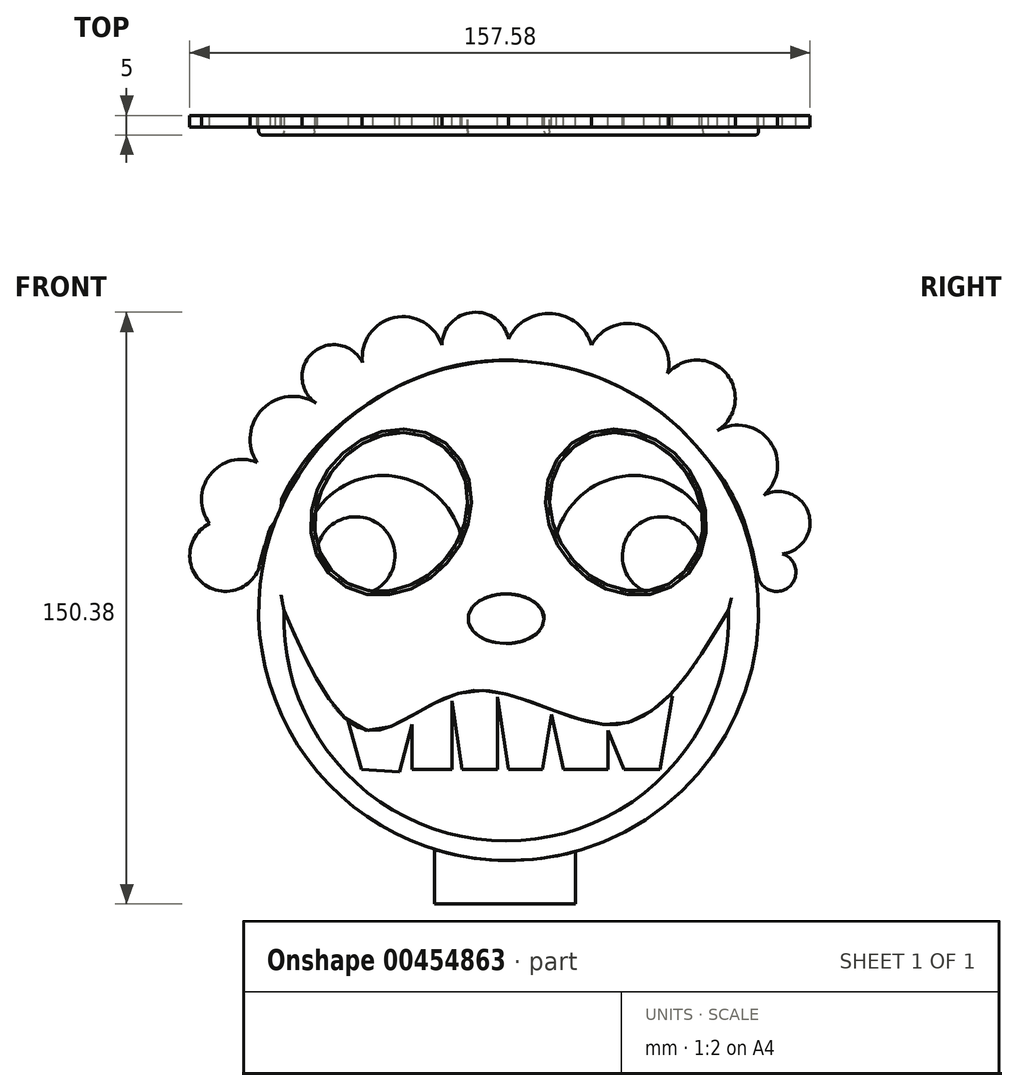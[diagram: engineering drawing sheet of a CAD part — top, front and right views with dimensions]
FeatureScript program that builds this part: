
annotation { "Feature Type Name" : "Feature", "Feature Type Description" : "" }
export const myFeature = defineFeature(function(context is Context, id is Id, definition is map)
    precondition{}
    {
        {
            var Q0;
            Q0=qCreatedBy(makeId("Front.planeOp"),FACE);
            var sketch = newSketch(context, id + "F0", { "sketchPlane" : qUnion([Q0])});
            skCircle(sketch, "E0", {"center": v(0, 0) * mm, "radius": 63.5 * mm});
            skEllipse(sketch, "E1", {"center": v(29.86, 25.05) * mm, "majorRadius": 21.26 * mm, "minorRadius": 18.23 * mm, "majorAxis": v(-0.62, 0.79)});
            skEllipse(sketch, "E2.MirrorC", {"center": v(-29.86, 25.05) * mm, "majorRadius": 21.26 * mm, "minorRadius": 18.23 * mm, "majorAxis": v(0.62, 0.79)});
            skArc(sketch, "E3", {"start": v(-58.71, 0) * mm, "mid": v(0, -58.71) * mm, "end": v(58.71, 0) * mm});
            skSolve(sketch);
        }
        {
            var Q0;
            Q0=makeQuery(id+"F0.imprint","IMPRINT",FACE,{"disambiguationData":[TD([[makeQuery(id+"F0.imprint","IMPRINT",EDGE,{"derivedFrom":sQuery(id+"F0.wireOp",EDGE,"E0")}),1.0]])]});
            extrude(context, id + "F1", {"entities" : qUnion([Q0]), "depth" : 5 * mm});
        }
        {
            var Q0;
            Q0=makeQuery(id+"F1.opExtrude","CAP_FACE",FACE,{"disambiguationData":[OSD([sQuery(id+"F0.wireOp",EDGE,"E0"),sQuery(id+"F0.wireOp",EDGE,"E1"),sQuery(id+"F0.wireOp",EDGE,"E2.MirrorC")])],"isStart":false});
            var sketch = newSketch(context, id + "F2", { "sketchPlane" : qUnion([Q0])});
            skArc(sketch, "E4", {"start": v(-57.08, 0) * mm, "mid": v(-0.64, -58.53) * mm, "end": v(55.8, 0) * mm});
            skEllipse(sketch, "E5", {"center": v(-0.64, -2.06) * mm, "majorRadius": 9.67 * mm, "minorRadius": 6.3 * mm, "majorAxis": v(1, 0)});
            skFitSpline(sketch, "E6", {"points": [v(-57.08, 0) * mm, v(-35.37, -30.5) * mm, v(-9.37, -20.35) * mm, v(27.73, -28.9) * mm, v(55.8, 0) * mm], "startDerivative": vector(78.01, -174.23) * mm, "endDerivative": vector(93.96, 156.78) * mm});
            skCircle(sketch, "E7", {"center": v(0, 59.87) * mm, "radius": 3.39 * mm});
            skSolve(sketch);
        }
        {
            var Q0;
            Q0=makeQuery(id+"F2.imprint","IMPRINT",FACE,{"disambiguationData":[TD([[makeQuery(id+"F2.imprint","IMPRINT",EDGE,{"derivedFrom":sQuery(id+"F2.wireOp",EDGE,"E5")}),1.0]])]});
            var Q1;
            Q1=makeQuery(id+"F2.imprint","IMPRINT",FACE,{"disambiguationData":[TD([[makeQuery(id+"F2.imprint","IMPRINT",EDGE,{"derivedFrom":sQuery(id+"F2.wireOp",EDGE,"E4")}),1.0]])]});
            extrude(context, id + "F3", {"entities" : qUnion([Q0, Q1]), "operationType" : NewBodyOperationType.REMOVE, "oppositeDirection" : true, "depth" : 5 * mm});
        }
        {
            var Q0;
            Q0=qCreatedBy(makeId("Front.planeOp"),FACE);
            var sketch = newSketch(context, id + "F4", { "sketchPlane" : qUnion([Q0])});
            skArc(sketch, "E8", {"start": v(-75.95, 22.14) * mm, "mid": v(-78.18, 7.4) * mm, "end": v(-63.59, 10.4) * mm});
            skArc(sketch, "E9", {"start": v(-63.27, 37.36) * mm, "mid": v(-74.74, 20.8) * mm, "end": v(-59.15, 33.56) * mm});
            skArc(sketch, "E10", {"start": v(-48.68, 52.58) * mm, "mid": v(-64.32, 48.79) * mm, "end": v(-59.15, 33.56) * mm});
            skArc(sketch, "E11", {"start": v(-36.32, 60.19) * mm, "mid": v(-48.64, 66.35) * mm, "end": v(-48.68, 52.58) * mm});
            skArc(sketch, "E12", {"start": v(-16.98, 67.48) * mm, "mid": v(-30.5, 74.02) * mm, "end": v(-36.32, 60.19) * mm});
            skArc(sketch, "E13", {"start": v(0, 69.07) * mm, "mid": v(-9.2, 75.78) * mm, "end": v(-16.98, 67.48) * mm});
            skArc(sketch, "E14", {"start": v(21.07, 67.48) * mm, "mid": v(11.08, 75.49) * mm, "end": v(0, 69.07) * mm});
            skArc(sketch, "E15", {"start": v(40.4, 60.19) * mm, "mid": v(33.94, 72.32) * mm, "end": v(21.07, 67.48) * mm});
            skArc(sketch, "E16", {"start": v(52.78, 45.6) * mm, "mid": v(55.26, 60.25) * mm, "end": v(40.4, 60.19) * mm});
            skArc(sketch, "E17", {"start": v(63.24, 28.17) * mm, "mid": v(66.89, 42.21) * mm, "end": v(52.78, 45.6) * mm});
            skArc(sketch, "E18", {"start": v(67.04, 14.53) * mm, "mid": v(76.28, 24.46) * mm, "end": v(63.24, 28.17) * mm});
            skArc(sketch, "E19", {"start": v(63.24, 9.14) * mm, "mid": v(72.07, 6.94) * mm, "end": v(67.04, 14.53) * mm});
            skFitSpline(sketch, "E20", {"points": [v(-63.59, 10.4) * mm, v(-50.59, 39.58) * mm, v(0, 63.68) * mm, v(52.46, 36.1) * mm, v(63.24, 9.14) * mm], "startDerivative": vector(35.5, 136.83) * mm, "endDerivative": vector(26.17, -129.5) * mm});
            skLineSegment(sketch, "E21", {"start": v(-24.59, -28.9) * mm, "end": v(-24.59, -40.32) * mm});
            skLineSegment(sketch, "E22", {"start": v(-24.59, -40.32) * mm, "end": v(-14.44, -40.32) * mm});
            skLineSegment(sketch, "E23", {"start": v(-14.44, -40.32) * mm, "end": v(-14.44, -22.88) * mm});
            skLineSegment(sketch, "E24", {"start": v(-14.44, -22.88) * mm, "end": v(-11.8, -40.32) * mm});
            skLineSegment(sketch, "E25", {"start": v(-11.8, -40.32) * mm, "end": v(-2.8, -40.32) * mm});
            skLineSegment(sketch, "E26", {"start": v(-2.8, -40.32) * mm, "end": v(-2.8, -21.95) * mm});
            skLineSegment(sketch, "E27", {"start": v(-2.8, -21.95) * mm, "end": v(0, -40.32) * mm});
            skLineSegment(sketch, "E28", {"start": v(0, -40.32) * mm, "end": v(8.6, -40.32) * mm});
            skLineSegment(sketch, "E29", {"start": v(8.6, -40.32) * mm, "end": v(10.92, -26.37) * mm});
            skLineSegment(sketch, "E30", {"start": v(10.92, -26.37) * mm, "end": v(13.91, -40.32) * mm});
            skLineSegment(sketch, "E31", {"start": v(13.91, -40.32) * mm, "end": v(25.2, -40.32) * mm});
            skLineSegment(sketch, "E32", {"start": v(25.2, -40.32) * mm, "end": v(25.2, -30.5) * mm});
            skLineSegment(sketch, "E33", {"start": v(25.2, -30.5) * mm, "end": v(29.26, -40.32) * mm});
            skPoint(sketch, "E33.endSnap0", {"position": v(-7.3, -40.32) * mm});
            skLineSegment(sketch, "E34", {"start": v(29.26, -40.32) * mm, "end": v(38.4, -40.32) * mm});
            skLineSegment(sketch, "E35", {"start": v(38.4, -40.32) * mm, "end": v(41.68, -21.61) * mm});
            skLineSegment(sketch, "E36", {"start": v(41.68, -21.61) * mm, "end": v(-36, -17.17) * mm});
            skLineSegment(sketch, "E37", {"start": v(-36, -17.17) * mm, "end": v(-43.44, -18.3) * mm});
            skLineSegment(sketch, "E38", {"start": v(-43.44, -18.3) * mm, "end": v(-37.41, -40.32) * mm});
            skLineSegment(sketch, "E39", {"start": v(-24.59, -28.9) * mm, "end": v(-27.76, -40.95) * mm});
            skLineSegment(sketch, "E40", {"start": v(-37.41, -40.32) * mm, "end": v(-27.76, -40.95) * mm});
            skCircle(sketch, "E41", {"center": v(-38.86, 13.9) * mm, "radius": 9.96 * mm});
            skCircle(sketch, "E42", {"center": v(-31.88, 13.9) * mm, "radius": 20.42 * mm});
            skCircle(sketch, "E43.MirrorC", {"center": v(31.88, 13.9) * mm, "radius": 20.42 * mm});
            skCircle(sketch, "E44.MirrorC", {"center": v(38.86, 13.9) * mm, "radius": 9.96 * mm});
            skLineSegment(sketch, "E45.bottom", {"start": v(-18.88, -60.93) * mm, "end": v(16.95, -60.93) * mm});
            skLineSegment(sketch, "E45.top", {"start": v(-18.88, -74.56) * mm, "end": v(16.95, -74.56) * mm});
            skLineSegment(sketch, "E45.left", {"start": v(-18.88, -60.93) * mm, "end": v(-18.88, -74.56) * mm});
            skLineSegment(sketch, "E45.right", {"start": v(16.95, -60.93) * mm, "end": v(16.95, -74.56) * mm});
            skCircle(sketch, "E46", {"center": v(0, 59.87) * mm, "radius": 3.24 * mm});
            skSolve(sketch);
        }
        {
            var Q0;
            Q0 = qSketchRegion(id + "F4", true);
            extrude(context, id + "F5", {"entities" : qUnion([Q0]), "operationType" : NewBodyOperationType.ADD, "depth" : 3 * mm});
        }
        {
            var Q0;
            Q0 = qSketchRegion(id + "F4", true);
            extrude(context, id + "F6", {"entities" : qUnion([Q0]), "operationType" : NewBodyOperationType.ADD, "depth" : 3 * mm});
        }
        {
            var Q0;
            Q0=makeQuery(id+"F1.opExtrude","CAP_EDGE",EDGE,{"disambiguationData":[OSD([sQuery(id+"F0.wireOp",EDGE,"E0")])],"isStart":false});
            fillet(context, id + "F7", {"entities" : qUnion([Q0]), "radius" : 1 * mm, "tangentPropagation" : true, "allowEdgeOverflow" : false});
        }
        {
            var Q0;
            Q0=makeQuery(id+"F1.opExtrude","CAP_FACE",FACE,{"disambiguationData":[OSD([sQuery(id+"F0.wireOp",EDGE,"E0"),sQuery(id+"F0.wireOp",EDGE,"E1"),sQuery(id+"F0.wireOp",EDGE,"E2.MirrorC")])],"isStart":false});
            fillet(context, id + "F8", {"entities" : qUnion([Q0]), "radius" : 1 * mm, "tangentPropagation" : true, "allowEdgeOverflow" : false});
        }
        {
            var Q0;
            Q0 = qSketchRegion(id + "F4", true);
            extrude(context, id + "F9", {"entities" : qUnion([Q0]), "operationType" : NewBodyOperationType.ADD, "depth" : 3 * mm});
        }
    });
